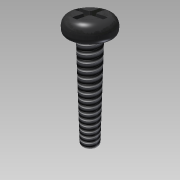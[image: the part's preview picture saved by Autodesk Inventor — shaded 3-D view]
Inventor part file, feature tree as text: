
AUTODESK INVENTOR PART (.ipt)
format: ipt  version: 2014 (Build 180170000, 170)  size: 150,528 bytes
history: native  units: in
note: dims shown in document units (in); Inventor stores cm internally (conversion verified against a paired STEP export)
features: extrude x3, fillet x3, sketch x3, thread x1, chamfer x1
ambient origin geometry x8: Origin, YZ Plane, XZ Plane, XY Plane, X Axis, Y Axis, Z Axis, Center Point
bodies: Solid1 (feature_tree)
feature tree (11):
  extrude  "Extrusion1"  Depth=0.6299in TaperAngle=0.0deg
  extrude  "Extrusion2"  Depth=0.0866in TaperAngle=0.0deg
  fillet  "Fillet1"  Radius=0.0276in
  fillet  "Fillet2"  Radius=0.0472in
  extrude  "Extrusion3"  Depth=0.3937in
  fillet  "Fillet3"  Radius=0.1575in
  thread  "Thread1"  [1 undecoded]
  chamfer  "Chamfer1"  Distance=0.0787in
  sketch  "Sketch1"  dims[d0=0.1142in d1=0.6299in d2=0.0in]
  sketch  "Sketch2"  dims[d3=0.2283in d4=0.0866in d5=0.0in d6=0.0276in d7=0.0472in]
  sketch  "Sketch3"  dims[d8=0.0276in d9=0.1575in d10=0.1575in d11=0.0276in d12=0.0787in d13=-0.0687in d14=0.0118in d15=0.3937in d16=0.0in d17=0.0197in d18=0.0787in d19=45.0deg]
note: 1 required parameter value undecoded (feature->parameter linkage not recoverable at this tier; creation-order binding heuristic only, values carry confidence <= 0.55)
